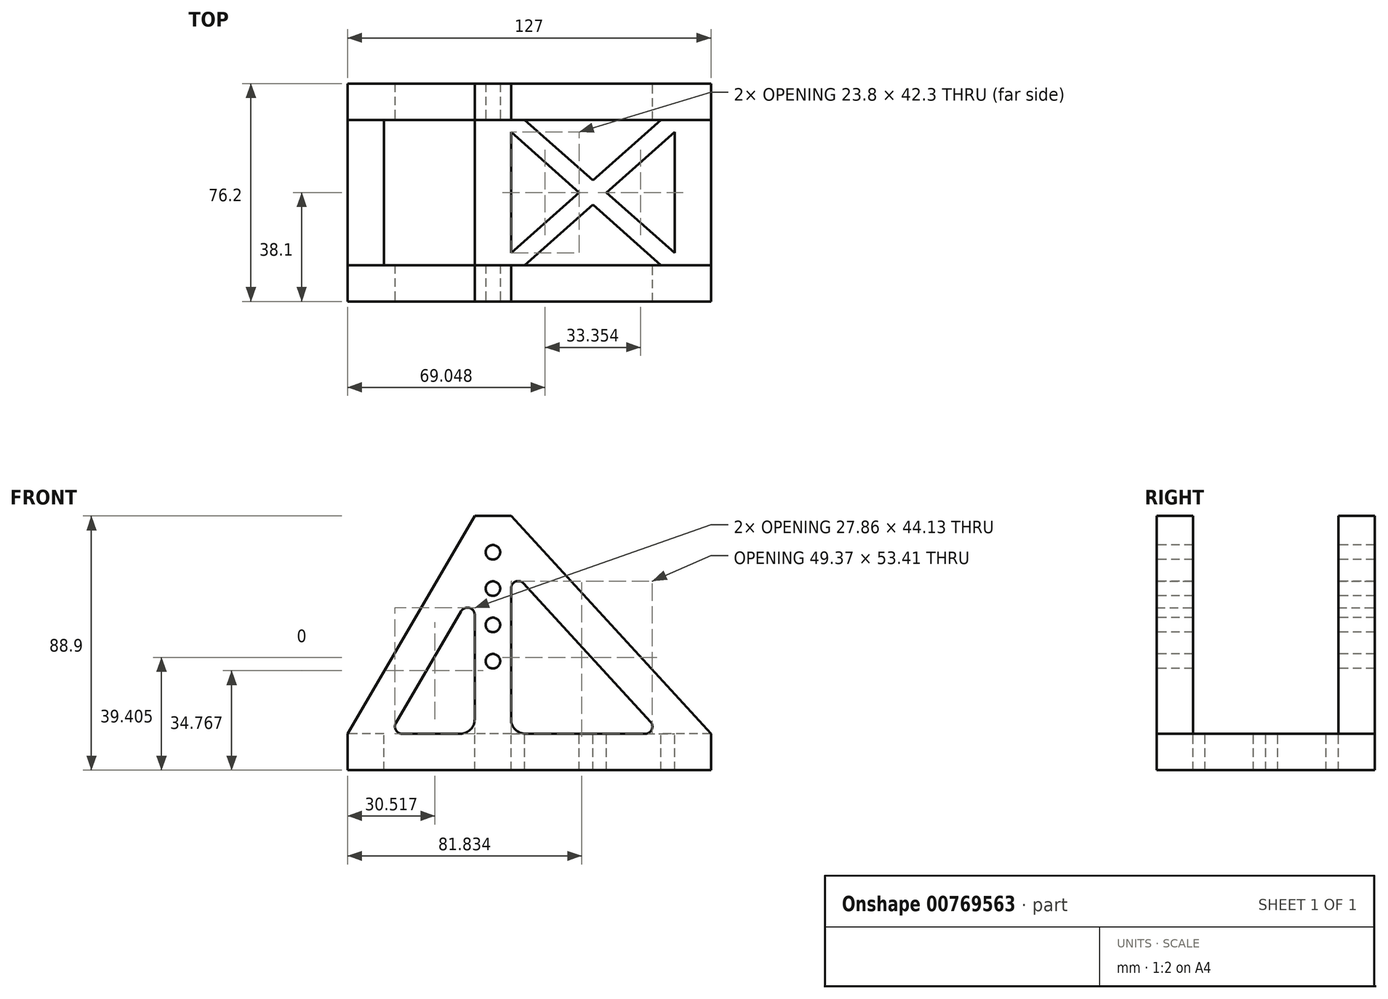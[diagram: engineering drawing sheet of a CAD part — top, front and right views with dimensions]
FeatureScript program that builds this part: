
annotation { "Feature Type Name" : "Feature", "Feature Type Description" : "" }
export const myFeature = defineFeature(function(context is Context, id is Id, definition is map)
    precondition{}
    {
        {
            var Q0;
            Q0=qCreatedBy(makeId("Front.planeOp"),FACE);
            var sketch = newSketch(context, id + "F0", { "sketchPlane" : qUnion([Q0])});
            skLineSegment(sketch, "E0", {"start": v(0, 0) * mm, "end": v(76.2, 0) * mm});
            skLineSegment(sketch, "E1", {"start": v(76.2, 0) * mm, "end": v(-50.8, 0) * mm});
            skLineSegment(sketch, "E2", {"start": v(-50.8, 0) * mm, "end": v(-50.8, 12.7) * mm});
            skLineSegment(sketch, "E3", {"start": v(-36.1, 12.7) * mm, "end": v(-6.35, 12.7) * mm});
            skLineSegment(sketch, "E4", {"start": v(76.2, 12.7) * mm, "end": v(76.2, 0) * mm});
            skLineSegment(sketch, "E5", {"start": v(0, 0) * mm, "end": v(0, 88.9) * mm, "construction": true});
            skLineSegment(sketch, "E6.bottom", {"start": v(6.35, 88.9) * mm, "end": v(-6.35, 88.9) * mm});
            skLineSegment(sketch, "E6.top", {"start": v(6.35, 88.9) * mm, "end": v(-6.35, 88.9) * mm});
            skLineSegment(sketch, "E6.left", {"start": v(6.35, 88.9) * mm, "end": v(6.35, 88.9) * mm});
            skLineSegment(sketch, "E6.right", {"start": v(-6.35, 88.9) * mm, "end": v(-6.35, 88.9) * mm});
            skPoint(sketch, "E6.middle", {"position": v(0, 88.9) * mm});
            skLineSegment(sketch, "E7", {"start": v(-6.35, 88.9) * mm, "end": v(-50.8, 12.7) * mm});
            skLineSegment(sketch, "E8", {"start": v(6.35, 88.9) * mm, "end": v(76.2, 12.7) * mm});
            skLineSegment(sketch, "E9", {"start": v(-6.35, 63.7) * mm, "end": v(-6.35, 12.7) * mm});
            skLineSegment(sketch, "E10.trimOffspring", {"start": v(-6.35, 63.7) * mm, "end": v(-36.1, 12.7) * mm});
            skLineSegment(sketch, "E11.trimOffspring", {"start": v(6.35, 70.1) * mm, "end": v(58.97, 12.7) * mm});
            skLineSegment(sketch, "E12.trimOffspring", {"start": v(6.35, 70.1) * mm, "end": v(6.35, 12.7) * mm});
            skLineSegment(sketch, "E13.trimOffspring", {"start": v(6.35, 12.7) * mm, "end": v(58.97, 12.7) * mm});
            skPoint(sketch, "E14.orphan", {"position": v(6.35, 0) * mm});
            skPoint(sketch, "E15", {"position": v(0, 76.2) * mm});
            skPoint(sketch, "E16", {"position": v(0, 63.5) * mm});
            skPoint(sketch, "E17", {"position": v(0, 50.8) * mm});
            skPoint(sketch, "E18", {"position": v(0, 38.1) * mm});
            skCircle(sketch, "E19", {"center": v(0, 38.1) * mm, "radius": 2.25 * mm});
            skCircle(sketch, "E20", {"center": v(0, 50.8) * mm, "radius": 2.25 * mm});
            skCircle(sketch, "E21", {"center": v(0, 63.5) * mm, "radius": 2.25 * mm});
            skCircle(sketch, "E22", {"center": v(0, 76.2) * mm, "radius": 2.25 * mm});
            skSolve(sketch);
        }
        {
            var Q0;
            Q0=qSketchRegion(id+"F0",true);
            extrude(context, id + "F1", {"entities" : qUnion([Q0]), "depth" : 76.2 * mm, "offsetDistance" : 25.4 * mm});
        }
        {
            var Q0;
            Q0=makeQuery(id+"F1.opExtrude","SWEPT_FACE",FACE,{"disambiguationData":[OSD([sQuery(id+"F0.wireOp",EDGE,"E2")])]});
            var sketch = newSketch(context, id + "F2", { "sketchPlane" : qUnion([Q0])});
            skLineSegment(sketch, "E23.bottom", {"start": v(0, 0) * mm, "end": v(76.2, 0) * mm});
            skLineSegment(sketch, "E23.top", {"start": v(0, 12.7) * mm, "end": v(76.2, 12.7) * mm});
            skLineSegment(sketch, "E23.left", {"start": v(0, 0) * mm, "end": v(0, 12.7) * mm});
            skLineSegment(sketch, "E23.right", {"start": v(76.2, 0) * mm, "end": v(76.2, 12.7) * mm});
            skLineSegment(sketch, "E24", {"start": v(76.2, 12.7) * mm, "end": v(63.5, 12.7) * mm});
            skLineSegment(sketch, "E25", {"start": v(12.7, 12.7) * mm, "end": v(12.7, 88.9) * mm});
            skLineSegment(sketch, "E26", {"start": v(12.7, 88.9) * mm, "end": v(63.5, 88.9) * mm});
            skLineSegment(sketch, "E27", {"start": v(63.5, 88.9) * mm, "end": v(63.5, 12.7) * mm});
            skSolve(sketch);
        }
        {
            var Q0;
            {var subQ2=sQuery(id+"F2.wireOp",EDGE,"E25");Q0=makeQuery(id+"F2.imprint","IMPRINT",FACE,{"disambiguationData":[TD([[makeQuery(id+"F2.imprint","IMPRINT",EDGE,{"derivedFrom":subQ2}),-1.0]])]});}
            extrude(context, id + "F3", {"entities" : qUnion([Q0]), "operationType" : NewBodyOperationType.REMOVE, "oppositeDirection" : true, "depth" : 254 * mm, "offsetDistance" : 25.4 * mm});
        }
        {
            var Q0;
            Q0=makeQuery(id+"F3.boolean.opBoolean","MERGE",FACE,{"derivedFrom":[makeQuery(id+"F1.opExtrude","SWEPT_FACE",FACE,{"disambiguationData":[OSD([sQuery(id+"F0.wireOp",EDGE,"E3")])]}),makeQuery(id+"F1.opExtrude","SWEPT_FACE",FACE,{"disambiguationData":[OSD([sQuery(id+"F0.wireOp",EDGE,"E13.trimOffspring")])]}),makeQuery(id+"F3.opExtrude","SWEPT_FACE",FACE,{"disambiguationData":[OSD([sQuery(id+"F2.wireOp",EDGE,"E23.top")])]})]});
            var sketch = newSketch(context, id + "F4", { "sketchPlane" : qUnion([Q0])});
            skLineSegment(sketch, "E28.bottom", {"start": v(-50.8, -12.7) * mm, "end": v(76.2, -12.7) * mm});
            skLineSegment(sketch, "E28.top", {"start": v(-50.8, -63.5) * mm, "end": v(76.2, -63.5) * mm});
            skLineSegment(sketch, "E28.left", {"start": v(-50.8, -12.7) * mm, "end": v(-50.8, -63.5) * mm});
            skLineSegment(sketch, "E28.right", {"start": v(76.2, -12.7) * mm, "end": v(76.2, -63.5) * mm});
            skLineSegment(sketch, "E29.0", {"start": v(63.5, -12.7) * mm, "end": v(63.5, -63.5) * mm});
            skLineSegment(sketch, "E30.0", {"start": v(-38.1, -12.7) * mm, "end": v(-38.1, -63.5) * mm});
            skLineSegment(sketch, "E31", {"start": v(6.35, -12.7) * mm, "end": v(6.35, -63.5) * mm});
            skLineSegment(sketch, "E32", {"start": v(6.35, -63.5) * mm, "end": v(-6.35, -63.5) * mm});
            skLineSegment(sketch, "E33", {"start": v(-6.35, -63.5) * mm, "end": v(-6.35, -12.7) * mm});
            skLineSegment(sketch, "E34.0", {"start": v(11.13, -63.5) * mm, "end": v(34.92, -42.35) * mm});
            skLineSegment(sketch, "E35.0", {"start": v(6.35, -59.25) * mm, "end": v(30.15, -38.1) * mm});
            skLineSegment(sketch, "E36.0", {"start": v(11.13, -12.7) * mm, "end": v(34.92, -33.85) * mm});
            skLineSegment(sketch, "E37.0", {"start": v(6.35, -16.95) * mm, "end": v(30.15, -38.1) * mm});
            skLineSegment(sketch, "E38.trimOffspring", {"start": v(34.92, -42.35) * mm, "end": v(58.72, -63.5) * mm});
            skLineSegment(sketch, "E39.trimOffspring", {"start": v(39.7, -38.1) * mm, "end": v(63.5, -16.95) * mm});
            skLineSegment(sketch, "E40.trimOffspring", {"start": v(39.7, -38.1) * mm, "end": v(63.5, -59.25) * mm});
            skLineSegment(sketch, "E41.trimOffspring", {"start": v(34.92, -33.85) * mm, "end": v(58.72, -12.7) * mm});
            skSolve(sketch);
        }
        {
            var Q0;
            {var subQ0=sQuery(id+"F4.wireOp",EDGE,"E36.0");Q0=makeQuery(id+"F4.imprint","IMPRINT",FACE,{"disambiguationData":[TD([[makeQuery(id+"F4.imprint","IMPRINT",EDGE,{"derivedFrom":subQ0}),1.0]])]});}
            var Q1;
            {var subQ0=sQuery(id+"F4.wireOp",EDGE,"E34.0");Q1=makeQuery(id+"F4.imprint","IMPRINT",FACE,{"disambiguationData":[TD([[makeQuery(id+"F4.imprint","IMPRINT",EDGE,{"derivedFrom":subQ0}),-1.0]])]});}
            var Q2;
            {var subQ32=sQuery(id+"F4.wireOp",EDGE,"E30.0");Q2=makeQuery(id+"F4.imprint","IMPRINT",FACE,{"disambiguationData":[TD([[makeQuery(id+"F4.imprint","IMPRINT",EDGE,{"derivedFrom":subQ32}),1.0]])]});}
            var Q3;
            {var subQ0=sQuery(id+"F4.wireOp",EDGE,"E35.0");Q3=makeQuery(id+"F4.imprint","IMPRINT",FACE,{"disambiguationData":[TD([[makeQuery(id+"F4.imprint","IMPRINT",EDGE,{"derivedFrom":subQ0}),1.0]])]});}
            var Q4;
            {var subQ0=sQuery(id+"F4.wireOp",EDGE,"E39.trimOffspring");Q4=makeQuery(id+"F4.imprint","IMPRINT",FACE,{"disambiguationData":[TD([[makeQuery(id+"F4.imprint","IMPRINT",EDGE,{"derivedFrom":subQ0}),-1.0]])]});}
            extrude(context, id + "F5", {"entities" : qUnion([Q0, Q1, Q2, Q3, Q4]), "operationType" : NewBodyOperationType.REMOVE, "oppositeDirection" : true, "depth" : 25.4 * mm, "offsetDistance" : 25.4 * mm});
        }
        {
            var Q0;
            {var subQ1=sQuery(id+"F0.wireOp",EDGE,"E9");var subQ2=sQuery(id+"F0.wireOp",EDGE,"E3");Q0=makeQuery(id+"F3.boolean.opBoolean","SPLIT",EDGE,{"disambiguationData":[TD([makeQuery(id+"F3.opExtrude","SWEPT_FACE",FACE,{"disambiguationData":[OSD([sQuery(id+"F2.wireOp",EDGE,"E27")])]})])],"derivedFrom":makeQuery(id+"F1.opExtrude","SWEPT_EDGE",EDGE,{"disambiguationData":[OSD([subQ2,subQ1])]})});}
            var Q1;
            {var subQ0=sQuery(id+"F0.wireOp",EDGE,"E13.trimOffspring");var subQ1=sQuery(id+"F0.wireOp",EDGE,"E12.trimOffspring");Q1=makeQuery(id+"F3.boolean.opBoolean","SPLIT",EDGE,{"disambiguationData":[TD([makeQuery(id+"F3.opExtrude","SWEPT_FACE",FACE,{"disambiguationData":[OSD([sQuery(id+"F2.wireOp",EDGE,"E27")])]})])],"derivedFrom":makeQuery(id+"F1.opExtrude","SWEPT_EDGE",EDGE,{"disambiguationData":[OSD([subQ1,subQ0])]})});}
            var Q2;
            {var subQ1=sQuery(id+"F0.wireOp",EDGE,"E9");var subQ2=sQuery(id+"F0.wireOp",EDGE,"E3");Q2=makeQuery(id+"F3.boolean.opBoolean","SPLIT",EDGE,{"disambiguationData":[TD([makeQuery(id+"F3.opExtrude","SWEPT_FACE",FACE,{"disambiguationData":[OSD([sQuery(id+"F2.wireOp",EDGE,"E25")])]})])],"derivedFrom":makeQuery(id+"F1.opExtrude","SWEPT_EDGE",EDGE,{"disambiguationData":[OSD([subQ2,subQ1])]})});}
            var Q3;
            {var subQ0=sQuery(id+"F0.wireOp",EDGE,"E13.trimOffspring");var subQ1=sQuery(id+"F0.wireOp",EDGE,"E12.trimOffspring");Q3=makeQuery(id+"F3.boolean.opBoolean","SPLIT",EDGE,{"disambiguationData":[TD([makeQuery(id+"F3.opExtrude","SWEPT_FACE",FACE,{"disambiguationData":[OSD([sQuery(id+"F2.wireOp",EDGE,"E25")])]})])],"derivedFrom":makeQuery(id+"F1.opExtrude","SWEPT_EDGE",EDGE,{"disambiguationData":[OSD([subQ1,subQ0])]})});}
            fillet(context, id + "F6", {"entities" : qUnion([Q0, Q1, Q2, Q3]), "radius" : 5.08 * mm, "tangentPropagation" : true, "allowEdgeOverflow" : false});
        }
        {
            var Q0;
            {var subQ0=sQuery(id+"F0.wireOp",EDGE,"E10.trimOffspring");var subQ1=sQuery(id+"F0.wireOp",EDGE,"E9");Q0=makeQuery(id+"F3.boolean.opBoolean","SPLIT",EDGE,{"disambiguationData":[TD([makeQuery(id+"F3.opExtrude","SWEPT_FACE",FACE,{"disambiguationData":[OSD([sQuery(id+"F2.wireOp",EDGE,"E27")])]})])],"derivedFrom":makeQuery(id+"F1.opExtrude","SWEPT_EDGE",EDGE,{"disambiguationData":[OSD([subQ1,subQ0])]})});}
            var Q1;
            {var subQ0=sQuery(id+"F0.wireOp",EDGE,"E13.trimOffspring");var subQ1=sQuery(id+"F0.wireOp",EDGE,"E11.trimOffspring");Q1=makeQuery(id+"F3.boolean.opBoolean","SPLIT",EDGE,{"disambiguationData":[TD([makeQuery(id+"F3.opExtrude","SWEPT_FACE",FACE,{"disambiguationData":[OSD([sQuery(id+"F2.wireOp",EDGE,"E27")])]})])],"derivedFrom":makeQuery(id+"F1.opExtrude","SWEPT_EDGE",EDGE,{"disambiguationData":[OSD([subQ1,subQ0])]})});}
            var Q2;
            {var subQ0=sQuery(id+"F0.wireOp",EDGE,"E12.trimOffspring");var subQ1=sQuery(id+"F0.wireOp",EDGE,"E11.trimOffspring");Q2=makeQuery(id+"F3.boolean.opBoolean","SPLIT",EDGE,{"disambiguationData":[TD([makeQuery(id+"F3.opExtrude","SWEPT_FACE",FACE,{"disambiguationData":[OSD([sQuery(id+"F2.wireOp",EDGE,"E27")])]})])],"derivedFrom":makeQuery(id+"F1.opExtrude","SWEPT_EDGE",EDGE,{"disambiguationData":[OSD([subQ1,subQ0])]})});}
            var Q3;
            {var subQ0=sQuery(id+"F0.wireOp",EDGE,"E12.trimOffspring");var subQ1=sQuery(id+"F0.wireOp",EDGE,"E11.trimOffspring");Q3=makeQuery(id+"F3.boolean.opBoolean","SPLIT",EDGE,{"disambiguationData":[TD([makeQuery(id+"F3.opExtrude","SWEPT_FACE",FACE,{"disambiguationData":[OSD([sQuery(id+"F2.wireOp",EDGE,"E25")])]})])],"derivedFrom":makeQuery(id+"F1.opExtrude","SWEPT_EDGE",EDGE,{"disambiguationData":[OSD([subQ1,subQ0])]})});}
            var Q4;
            {var subQ0=sQuery(id+"F0.wireOp",EDGE,"E10.trimOffspring");var subQ1=sQuery(id+"F0.wireOp",EDGE,"E9");Q4=makeQuery(id+"F3.boolean.opBoolean","SPLIT",EDGE,{"disambiguationData":[TD([makeQuery(id+"F3.opExtrude","SWEPT_FACE",FACE,{"disambiguationData":[OSD([sQuery(id+"F2.wireOp",EDGE,"E25")])]})])],"derivedFrom":makeQuery(id+"F1.opExtrude","SWEPT_EDGE",EDGE,{"disambiguationData":[OSD([subQ1,subQ0])]})});}
            var Q5;
            {var subQ0=sQuery(id+"F0.wireOp",EDGE,"E13.trimOffspring");var subQ2=sQuery(id+"F0.wireOp",EDGE,"E11.trimOffspring");Q5=makeQuery(id+"F3.boolean.opBoolean","SPLIT",EDGE,{"disambiguationData":[TD([makeQuery(id+"F3.opExtrude","SWEPT_FACE",FACE,{"disambiguationData":[OSD([sQuery(id+"F2.wireOp",EDGE,"E25")])]})])],"derivedFrom":makeQuery(id+"F1.opExtrude","SWEPT_EDGE",EDGE,{"disambiguationData":[OSD([subQ2,subQ0])]})});}
            var Q6;
            {var subQ1=sQuery(id+"F0.wireOp",EDGE,"E10.trimOffspring");var subQ2=sQuery(id+"F0.wireOp",EDGE,"E3");Q6=makeQuery(id+"F3.boolean.opBoolean","SPLIT",EDGE,{"disambiguationData":[TD([makeQuery(id+"F3.opExtrude","SWEPT_FACE",FACE,{"disambiguationData":[OSD([sQuery(id+"F2.wireOp",EDGE,"E25")])]})])],"derivedFrom":makeQuery(id+"F1.opExtrude","SWEPT_EDGE",EDGE,{"disambiguationData":[OSD([subQ2,subQ1])]})});}
            fillet(context, id + "F7", {"entities" : qUnion([Q0, Q1, Q2, Q3, Q4, Q5, Q6]), "radius" : 2.54 * mm, "tangentPropagation" : true, "allowEdgeOverflow" : false});
        }
        {
            var Q0;
            {var subQ1=sQuery(id+"F0.wireOp",EDGE,"E10.trimOffspring");var subQ2=sQuery(id+"F0.wireOp",EDGE,"E3");Q0=makeQuery(id+"F3.boolean.opBoolean","SPLIT",EDGE,{"disambiguationData":[TD([makeQuery(id+"F3.opExtrude","SWEPT_FACE",FACE,{"disambiguationData":[OSD([sQuery(id+"F2.wireOp",EDGE,"E27")])]})])],"derivedFrom":makeQuery(id+"F1.opExtrude","SWEPT_EDGE",EDGE,{"disambiguationData":[OSD([subQ2,subQ1])]})});}
            fillet(context, id + "F8", {"entities" : qUnion([Q0]), "radius" : 2.54 * mm, "tangentPropagation" : true, "allowEdgeOverflow" : false});
        }
        {
            var Q0;
            Q0=makeQuery(id+"F1.opExtrude","CAP_FACE",FACE,{"disambiguationData":[OSD([sQuery(id+"F0.wireOp",EDGE,"E1"),sQuery(id+"F0.wireOp",EDGE,"E2"),sQuery(id+"F0.wireOp",EDGE,"E3"),sQuery(id+"F0.wireOp",EDGE,"E4"),sQuery(id+"F0.wireOp",EDGE,"E6.top"),sQuery(id+"F0.wireOp",EDGE,"E7"),sQuery(id+"F0.wireOp",EDGE,"E8"),sQuery(id+"F0.wireOp",EDGE,"E9"),sQuery(id+"F0.wireOp",EDGE,"E10.trimOffspring"),sQuery(id+"F0.wireOp",EDGE,"E11.trimOffspring"),sQuery(id+"F0.wireOp",EDGE,"E12.trimOffspring"),sQuery(id+"F0.wireOp",EDGE,"E13.trimOffspring"),sQuery(id+"F0.wireOp",EDGE,"E19"),sQuery(id+"F0.wireOp",EDGE,"E20"),sQuery(id+"F0.wireOp",EDGE,"E21"),sQuery(id+"F0.wireOp",EDGE,"E22")])],"isStart":false});
            var sketch = newSketch(context, id + "F9", { "sketchPlane" : qUnion([Q0])});
            skCircle(sketch, "E42", {"center": v(0, 76.2) * mm, "radius": 2.54 * mm});
            skCircle(sketch, "E43", {"center": v(0, 63.5) * mm, "radius": 2.54 * mm});
            skCircle(sketch, "E44", {"center": v(0, 50.8) * mm, "radius": 2.54 * mm});
            skCircle(sketch, "E45", {"center": v(0, 38.1) * mm, "radius": 2.54 * mm});
            skSolve(sketch);
        }
        {
            var Q0;
            Q0=qSketchRegion(id+"F9",true);
            extrude(context, id + "F10", {"entities" : qUnion([Q0]), "operationType" : NewBodyOperationType.REMOVE, "oppositeDirection" : true, "depth" : 254 * mm, "offsetDistance" : 25.4 * mm});
        }
    });
